# Revit family: Haworth_Cielo_Pendant_FiveLight
name_source: partatom
category: Lighting Fixtures
revit_build: Autodesk Revit 2018 (Build: 20170223_1515(x64)
units: mm (PartAtom-declared; Revit-internal decimal feet)

## family parameters
Always vertical = Yes
Cut with Voids When Loaded = No
Host = Ceiling
Light Source = Yes
OmniClass Number = 23.80.70.11
OmniClass Title = Luminaries for Internal Lighting
Part Type = Normal
Room Calculation Point = No
Round Connector Dimension = Use Diameter
Shared = No

## types (1)
- LEP5-1810
    Apparent Load = 0 VA
    Assembly Code = D5020200
    Color Filter = 16777215
    Cords Finish = Haworth _ Metal _ Satin Aluminum_Grey-Cord TR-E05
    Description = Haworth Cielo Pendant with Five Lights
    Dimming Lamp Color Temperature Shift = <None>
    Emit Shape Visible in Rendering = No
    Emit from Circle Diameter = 1' - 6"
    Glass Finish = Haworth _ Glass _ Frosted
    Lamps Width = 1' - 6 1/2"
    Manufacturer = Haworth
    Max. Cords Length = 10' - 0"
    Min. Cords Length = 1' - 0"
    Model = LEP5-1810
    Photometric Web File = generic
    Revision Number = 1
    Size = Verify Final Dim. w/ Haworth
    Support Radius = 0' - 8 1/2"
    Tilt Angle = 90.00°
    URL = http://www.haworth.com
    URL - Product = https://www.haworth.com
    Warranty = http://www.haworth.com

## geometry (parser evidence)
native form markers: Sweep x6
no freeform markers — native parametric forms only
